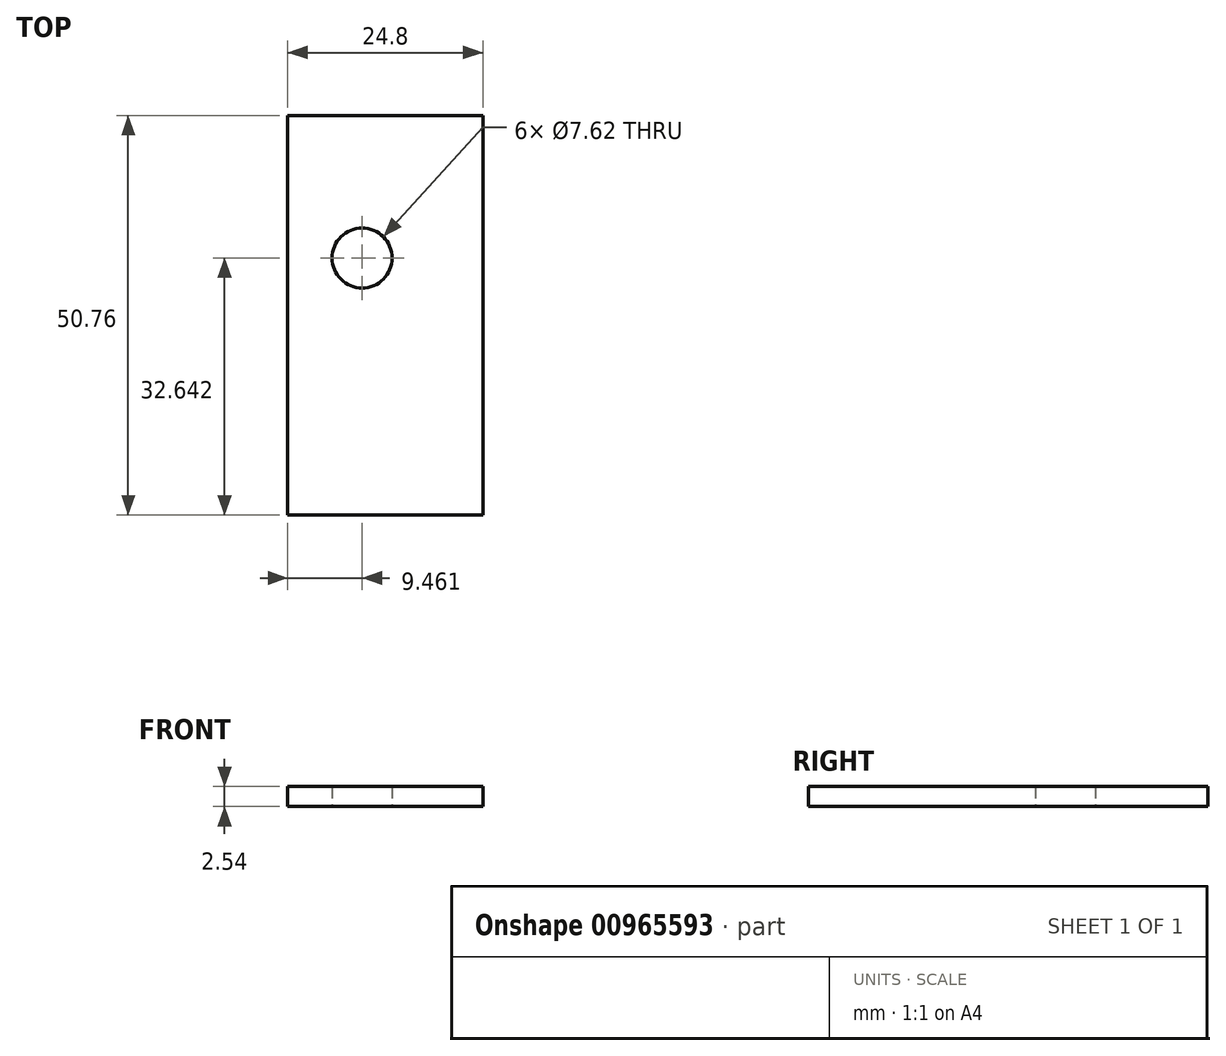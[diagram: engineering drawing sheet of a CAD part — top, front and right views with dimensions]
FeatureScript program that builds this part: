
annotation { "Feature Type Name" : "Feature", "Feature Type Description" : "" }
export const myFeature = defineFeature(function(context is Context, id is Id, definition is map)
    precondition{}
    {
        {
            var Q0;
            Q0=qCreatedBy(makeId("Top.planeOp"),FACE);
            var sketch = newSketch(context, id + "F0", { "sketchPlane" : qUnion([Q0])});
            skLineSegment(sketch, "E0.bottom", {"start": v(-71.54, 52.93) * mm, "end": v(-46.74, 52.93) * mm});
            skLineSegment(sketch, "E0.top", {"start": v(-71.54, 2.17) * mm, "end": v(-46.74, 2.17) * mm});
            skLineSegment(sketch, "E0.left", {"start": v(-71.54, 52.93) * mm, "end": v(-71.54, 2.17) * mm});
            skLineSegment(sketch, "E0.right", {"start": v(-46.74, 52.93) * mm, "end": v(-46.74, 2.17) * mm});
            skCircle(sketch, "E1", {"center": v(-62.08, 34.81) * mm, "radius": 3.81 * mm});
            skSolve(sketch);
        }
        {
            var Q0;
            Q0=makeQuery(id+"F0.imprint","IMPRINT",FACE,{"disambiguationData":[TD([[makeQuery(id+"F0.imprint","IMPRINT",EDGE,{"derivedFrom":sQuery(id+"F0.wireOp",EDGE,"E0.bottom")}),-1.0]])]});
            extrude(context, id + "F1", {"entities" : qUnion([Q0]), "depth" : 2.54 * mm, "offsetDistance" : 25.4 * mm});
        }
    });
